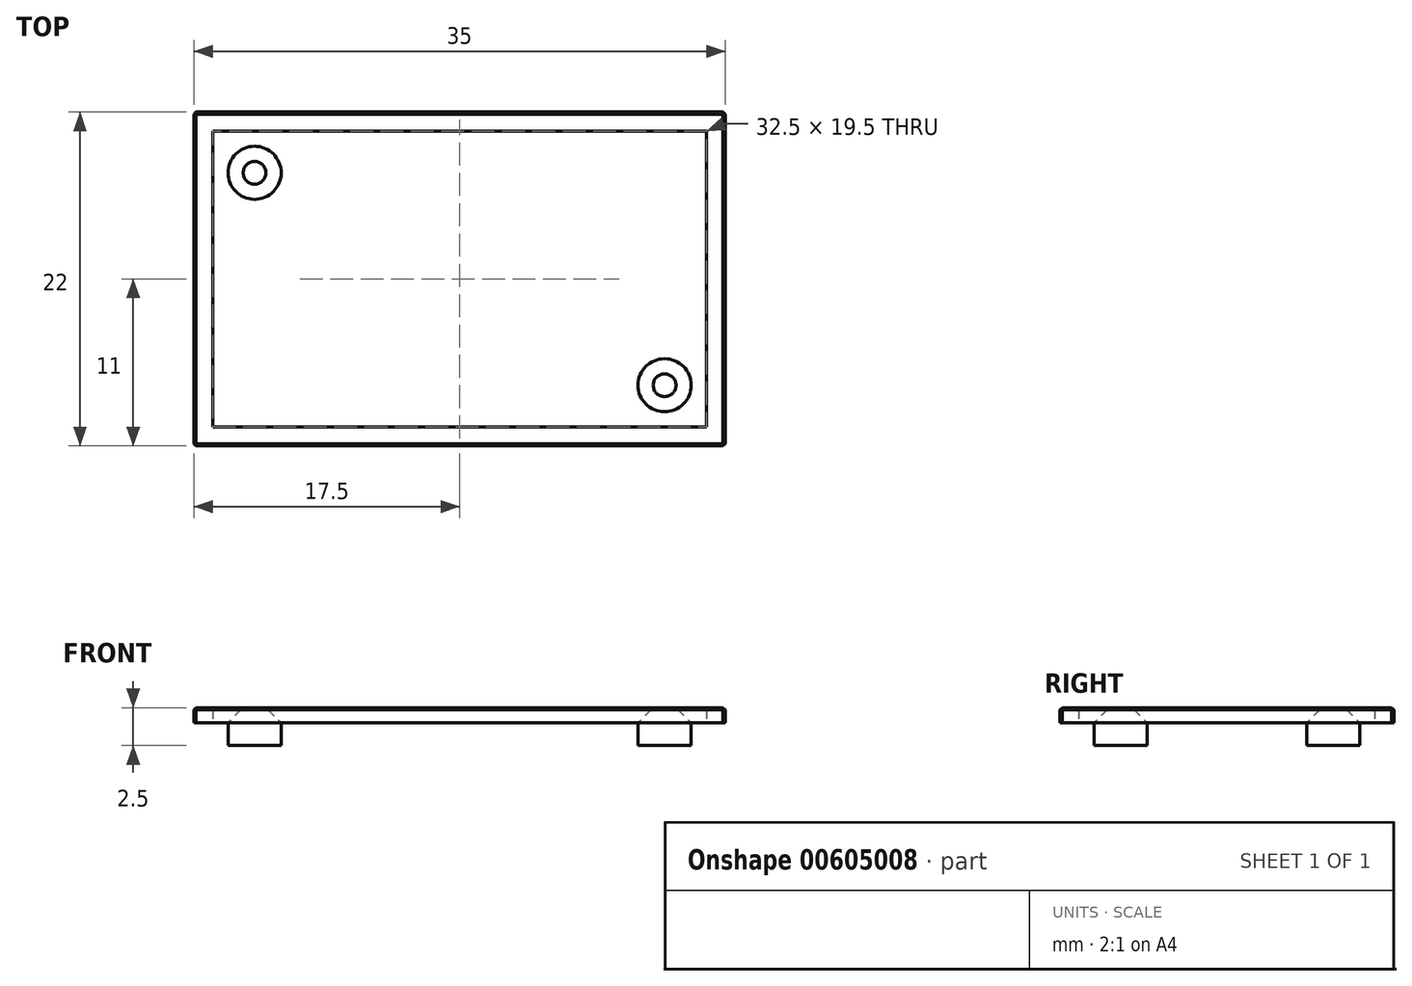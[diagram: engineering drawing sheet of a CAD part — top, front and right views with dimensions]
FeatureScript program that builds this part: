
annotation { "Feature Type Name" : "Feature", "Feature Type Description" : "" }
export const myFeature = defineFeature(function(context is Context, id is Id, definition is map)
    precondition{}
    {
        {
            var Q0;
            Q0=qCreatedBy(makeId("Top.planeOp"),FACE);
            var sketch = newSketch(context, id + "F0", { "sketchPlane" : qUnion([Q0])});
            skLineSegment(sketch, "E0.bottom", {"start": v(-17.5, 11) * mm, "end": v(17.5, 11) * mm});
            skLineSegment(sketch, "E0.top", {"start": v(-17.5, -11) * mm, "end": v(17.5, -11) * mm});
            skLineSegment(sketch, "E0.left", {"start": v(-17.5, 11) * mm, "end": v(-17.5, -11) * mm});
            skLineSegment(sketch, "E0.right", {"start": v(17.5, 11) * mm, "end": v(17.5, -11) * mm});
            skSolve(sketch);
        }
        {
            var Q0;
            Q0 = qSketchRegion(id + "F0", true);
            extrude(context, id + "F1", {"entities" : qUnion([Q0]), "depth" : 1 * mm, "offsetDistance" : 25 * mm});
        }
        {
            var Q0;
            Q0=makeQuery(id+"F1.opExtrude","CAP_EDGE",EDGE,{"disambiguationData":[OSD([sQuery(id+"F0.wireOp",EDGE,"E0.left")])],"isStart":false});
            var Q1;
            Q1=makeQuery(id+"F1.opExtrude","CAP_EDGE",EDGE,{"disambiguationData":[OSD([sQuery(id+"F0.wireOp",EDGE,"E0.bottom")])],"isStart":false});
            var Q2;
            Q2=makeQuery(id+"F1.opExtrude","CAP_EDGE",EDGE,{"disambiguationData":[OSD([sQuery(id+"F0.wireOp",EDGE,"E0.right")])],"isStart":false});
            var Q3;
            Q3=makeQuery(id+"F1.opExtrude","CAP_EDGE",EDGE,{"disambiguationData":[OSD([sQuery(id+"F0.wireOp",EDGE,"E0.top")])],"isStart":false});
            var Q4;
            Q4=makeQuery(id+"F1.opExtrude","SWEPT_EDGE",EDGE,{"disambiguationData":[OSD([sQuery(id+"F0.wireOp",EDGE,"E0.bottom"),sQuery(id+"F0.wireOp",EDGE,"E0.left")])]});
            var Q5;
            Q5=makeQuery(id+"F1.opExtrude","SWEPT_EDGE",EDGE,{"disambiguationData":[OSD([sQuery(id+"F0.wireOp",EDGE,"E0.bottom"),sQuery(id+"F0.wireOp",EDGE,"E0.right")])]});
            var Q6;
            Q6=makeQuery(id+"F1.opExtrude","SWEPT_EDGE",EDGE,{"disambiguationData":[OSD([sQuery(id+"F0.wireOp",EDGE,"E0.top"),sQuery(id+"F0.wireOp",EDGE,"E0.right")])]});
            var Q7;
            Q7=makeQuery(id+"F1.opExtrude","SWEPT_EDGE",EDGE,{"disambiguationData":[OSD([sQuery(id+"F0.wireOp",EDGE,"E0.top"),sQuery(id+"F0.wireOp",EDGE,"E0.left")])]});
            chamfer(context, id + "F2", {"entities" : qUnion([Q0, Q1, Q2, Q3, Q4, Q5, Q6, Q7]), "width" : 0.15 * mm, "tangentPropagation" : true});
        }
        {
            var Q0;
            Q0=makeQuery(id+"F1.opExtrude","CAP_FACE",FACE,{"disambiguationData":[OSD([sQuery(id+"F0.wireOp",EDGE,"E0.bottom"),sQuery(id+"F0.wireOp",EDGE,"E0.top"),sQuery(id+"F0.wireOp",EDGE,"E0.left"),sQuery(id+"F0.wireOp",EDGE,"E0.right")])],"isStart":true});
            var sketch = newSketch(context, id + "F3", { "sketchPlane" : qUnion([Q0])});
            skLineSegment(sketch, "E1.bottom", {"start": v(-16.25, 9.75) * mm, "end": v(16.25, 9.75) * mm});
            skLineSegment(sketch, "E1.top", {"start": v(-16.25, -9.75) * mm, "end": v(16.25, -9.75) * mm});
            skLineSegment(sketch, "E1.left", {"start": v(-16.25, 9.75) * mm, "end": v(-16.25, -9.75) * mm});
            skLineSegment(sketch, "E1.right", {"start": v(16.25, 9.75) * mm, "end": v(16.25, -9.75) * mm});
            skSolve(sketch);
        }
        {
            var Q0;
            Q0 = qSketchRegion(id + "F3", true);
            extrude(context, id + "F4", {"entities" : qUnion([Q0]), "operationType" : NewBodyOperationType.ADD, "depth" : 1.5 * mm, "offsetDistance" : 25 * mm});
        }
        {
            var Q0;
            Q0=makeQuery(id+"F4.opExtrude","CAP_FACE",FACE,{"disambiguationData":[OSD([sQuery(id+"F3.wireOp",EDGE,"E1.bottom"),sQuery(id+"F3.wireOp",EDGE,"E1.top"),sQuery(id+"F3.wireOp",EDGE,"E1.left"),sQuery(id+"F3.wireOp",EDGE,"E1.right")])],"isStart":false});
            var sketch = newSketch(context, id + "F5", { "sketchPlane" : qUnion([Q0])});
            skCircle(sketch, "E2", {"center": v(-13.5, 7) * mm, "radius": 1.75 * mm});
            skCircle(sketch, "E3.MirrorC", {"center": v(13.5, 7) * mm, "radius": 1.75 * mm});
            skCircle(sketch, "E4.MirrorC", {"center": v(-13.5, -7) * mm, "radius": 1.75 * mm});
            skCircle(sketch, "E5.MirrorC", {"center": v(13.5, -7) * mm, "radius": 1.75 * mm});
            skSolve(sketch);
        }
        {
            var Q0;
            Q0=makeQuery(id+"F5.imprint","IMPRINT",FACE,{"disambiguationData":[TD([[makeQuery(id+"F5.imprint","IMPRINT",EDGE,{"derivedFrom":sQuery(id+"F5.wireOp",EDGE,"E2")}),1.0]])]});
            var Q1;
            Q1=makeQuery(id+"F5.imprint","IMPRINT",FACE,{"disambiguationData":[TD([[makeQuery(id+"F5.imprint","IMPRINT",EDGE,{"derivedFrom":sQuery(id+"F5.wireOp",EDGE,"E4.MirrorC")}),-1.0]])]});
            var Q2;
            Q2=makeQuery(id+"F5.imprint","IMPRINT",FACE,{"disambiguationData":[TD([[makeQuery(id+"F5.imprint","IMPRINT",EDGE,{"derivedFrom":sQuery(id+"F5.wireOp",EDGE,"E5.MirrorC")}),1.0]])]});
            var Q3;
            Q3=makeQuery(id+"F5.imprint","IMPRINT",FACE,{"disambiguationData":[TD([[makeQuery(id+"F5.imprint","IMPRINT",EDGE,{"derivedFrom":sQuery(id+"F5.wireOp",EDGE,"E3.MirrorC")}),-1.0]])]});
            extrude(context, id + "F6", {"entities" : qUnion([Q0, Q1, Q2, Q3]), "operationType" : NewBodyOperationType.REMOVE, "oppositeDirection" : true, "depth" : 25 * mm, "offsetDistance" : 25 * mm});
        }
        {
            var Q0;
            Q0=makeQuery(id+"F6.boolean.opBoolean","INTERSECT",EDGE,{"derivedFrom":[makeQuery(id+"F1.opExtrude","CAP_FACE",FACE,{"disambiguationData":[OSD([sQuery(id+"F0.wireOp",EDGE,"E0.bottom"),sQuery(id+"F0.wireOp",EDGE,"E0.top"),sQuery(id+"F0.wireOp",EDGE,"E0.left"),sQuery(id+"F0.wireOp",EDGE,"E0.right")])],"isStart":false}),makeQuery(id+"F6.opExtrude","SWEPT_FACE",FACE,{"disambiguationData":[OSD([sQuery(id+"F5.wireOp",EDGE,"E4.MirrorC")])]})]});
            var Q1;
            Q1=makeQuery(id+"F6.boolean.opBoolean","INTERSECT",EDGE,{"derivedFrom":[makeQuery(id+"F1.opExtrude","CAP_FACE",FACE,{"disambiguationData":[OSD([sQuery(id+"F0.wireOp",EDGE,"E0.bottom"),sQuery(id+"F0.wireOp",EDGE,"E0.top"),sQuery(id+"F0.wireOp",EDGE,"E0.left"),sQuery(id+"F0.wireOp",EDGE,"E0.right")])],"isStart":false}),makeQuery(id+"F6.opExtrude","SWEPT_FACE",FACE,{"disambiguationData":[OSD([sQuery(id+"F5.wireOp",EDGE,"E5.MirrorC")])]})]});
            var Q2;
            Q2=makeQuery(id+"F6.boolean.opBoolean","INTERSECT",EDGE,{"derivedFrom":[makeQuery(id+"F1.opExtrude","CAP_FACE",FACE,{"disambiguationData":[OSD([sQuery(id+"F0.wireOp",EDGE,"E0.bottom"),sQuery(id+"F0.wireOp",EDGE,"E0.top"),sQuery(id+"F0.wireOp",EDGE,"E0.left"),sQuery(id+"F0.wireOp",EDGE,"E0.right")])],"isStart":false}),makeQuery(id+"F6.opExtrude","SWEPT_FACE",FACE,{"disambiguationData":[OSD([sQuery(id+"F5.wireOp",EDGE,"E3.MirrorC")])]})]});
            var Q3;
            Q3=makeQuery(id+"F6.boolean.opBoolean","INTERSECT",EDGE,{"derivedFrom":[makeQuery(id+"F1.opExtrude","CAP_FACE",FACE,{"disambiguationData":[OSD([sQuery(id+"F0.wireOp",EDGE,"E0.bottom"),sQuery(id+"F0.wireOp",EDGE,"E0.top"),sQuery(id+"F0.wireOp",EDGE,"E0.left"),sQuery(id+"F0.wireOp",EDGE,"E0.right")])],"isStart":false}),makeQuery(id+"F6.opExtrude","SWEPT_FACE",FACE,{"disambiguationData":[OSD([sQuery(id+"F5.wireOp",EDGE,"E2")])]})]});
            chamfer(context, id + "F7", {"entities" : qUnion([Q0, Q1, Q2, Q3]), "width" : 1 * mm, "tangentPropagation" : true});
        }
    });
